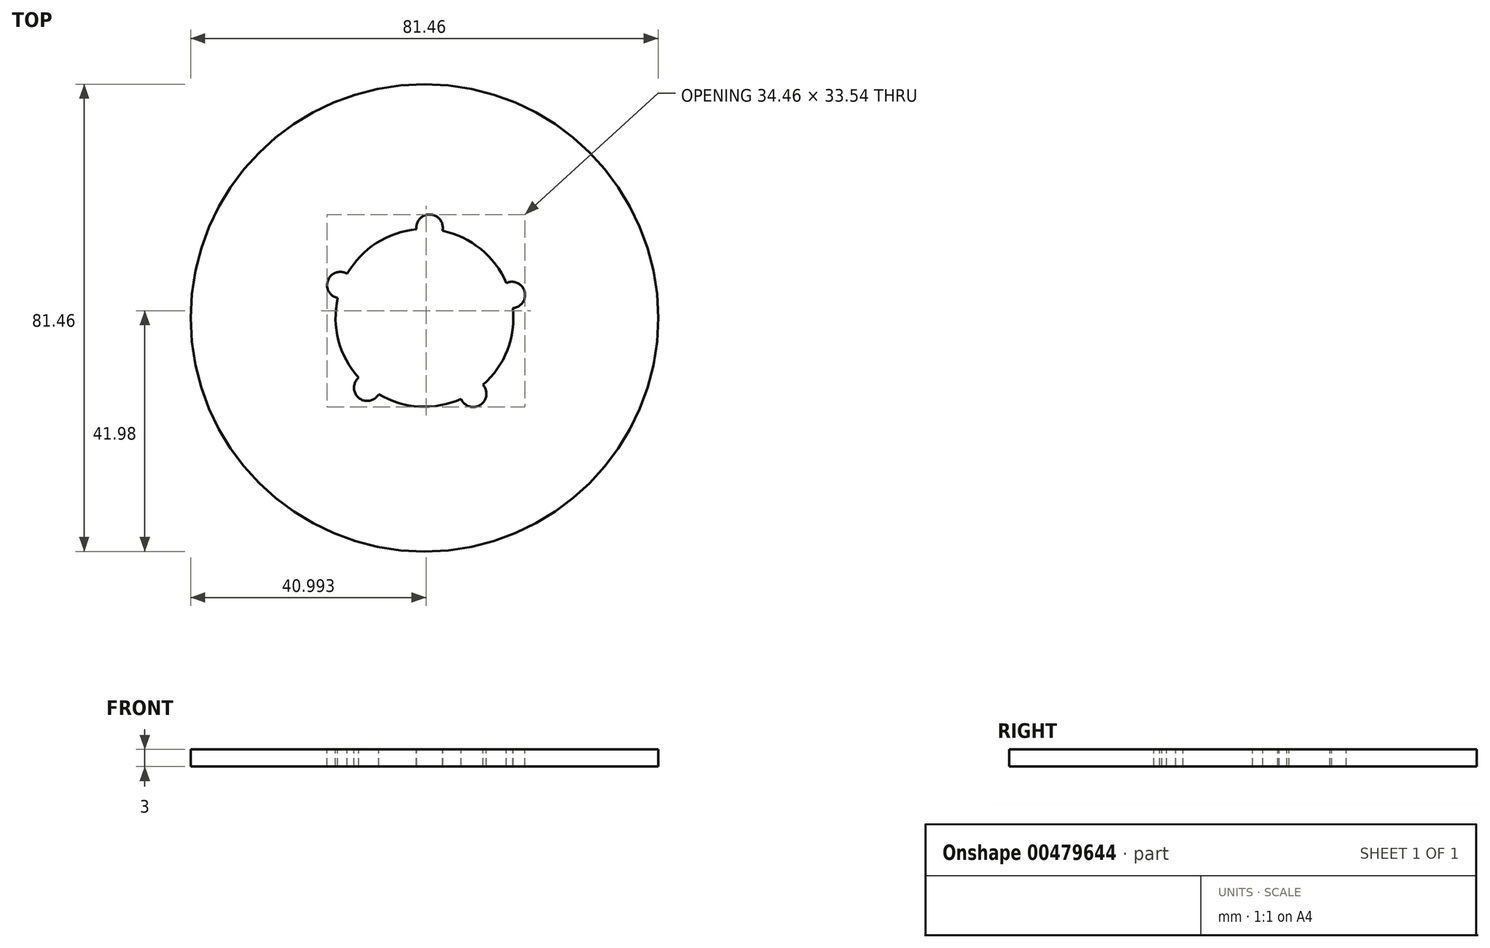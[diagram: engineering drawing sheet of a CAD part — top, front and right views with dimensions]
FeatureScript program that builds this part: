
annotation { "Feature Type Name" : "Feature", "Feature Type Description" : "" }
export const myFeature = defineFeature(function(context is Context, id is Id, definition is map)
    precondition{}
    {
        {
            var Q0;
            Q0=qCreatedBy(makeId("Top.planeOp"),FACE);
            var sketch = newSketch(context, id + "F0", { "sketchPlane" : qUnion([Q0])});
            skCircle(sketch, "E0", {"center": v(0, 0) * mm, "radius": 40.73 * mm});
            skSolve(sketch);
        }
        {
            var Q0;
            Q0 = qSketchRegion(id + "F0", true);
            extrude(context, id + "F1", {"entities" : qUnion([Q0]), "depth" : 3 * mm});
        }
        {
            var Q0;
            Q0=makeQuery(id+"F1.opExtrude","CAP_FACE",FACE,{"disambiguationData":[OSD([sQuery(id+"F0.wireOp",EDGE,"E0")])],"isStart":false});
            var sketch = newSketch(context, id + "F2", { "sketchPlane" : qUnion([Q0])});
            skCircle(sketch, "E1", {"center": v(0, 0) * mm, "radius": 12.35 * mm});
            skSolve(sketch);
        }
        {
            var Q0;
            Q0 = qSketchRegion(id + "F2", true);
            extrude(context, id + "F3", {"entities" : qUnion([Q0]), "operationType" : NewBodyOperationType.REMOVE, "oppositeDirection" : true, "depth" : 5 * mm});
        }
        {
            var Q0;
            Q0=makeQuery(id+"F1.opExtrude","CAP_FACE",FACE,{"disambiguationData":[OSD([sQuery(id+"F0.wireOp",EDGE,"E0")])],"isStart":false});
            var sketch = newSketch(context, id + "F4", { "sketchPlane" : qUnion([Q0])});
            skCircle(sketch, "E2", {"center": v(0, 0) * mm, "radius": 15.5 * mm});
            skSolve(sketch);
        }
        {
            var Q0;
            Q0 = qSketchRegion(id + "F4", true);
            var Q1;
            Q1 = qSketchRegion(id + "F6", true);
            extrude(context, id + "F5", {"entities" : qUnion([Q0, Q1]), "operationType" : NewBodyOperationType.REMOVE, "oppositeDirection" : true, "depth" : 3 * mm});
        }
        {
            var Q0;
            Q0=makeQuery(id+"F1.opExtrude","CAP_FACE",FACE,{"disambiguationData":[OSD([sQuery(id+"F0.wireOp",EDGE,"E0")])],"isStart":false});
            var sketch = newSketch(context, id + "F6", { "sketchPlane" : qUnion([Q0])});
            skCircle(sketch, "E3", {"center": v(0, 0) * mm, "radius": 15.75 * mm});
            skSolve(sketch);
        }
        {
            var Q0;
            Q0=makeQuery(id+"F6.imprint","IMPRINT",FACE,{"disambiguationData":[TD([[makeQuery(id+"F6.imprint","IMPRINT",EDGE,{"derivedFrom":sQuery(id+"F6.wireOp",EDGE,"E3")}),-1.0]])]});
            var sketch = newSketch(context, id + "F7", { "sketchPlane" : qUnion([Q0])});
            skCircle(sketch, "E4", {"center": v(15.23, 4) * mm, "radius": 2.3 * mm});
            skCircle(sketch, "E5", {"center": v(8.5, -13.24) * mm, "radius": 2.3 * mm});
            skCircle(sketch, "E6", {"center": v(-9.98, -12.18) * mm, "radius": 2.3 * mm});
            skCircle(sketch, "E7", {"center": v(-14.67, 5.72) * mm, "radius": 2.3 * mm});
            skCircle(sketch, "E8", {"center": v(0.9, 15.73) * mm, "radius": 2.3 * mm});
            skSolve(sketch);
        }
        {
            var Q0;
            Q0 = qSketchRegion(id + "F7", true);
            extrude(context, id + "F8", {"entities" : qUnion([Q0]), "operationType" : NewBodyOperationType.REMOVE, "oppositeDirection" : true, "depth" : 25 * mm});
        }
    });
